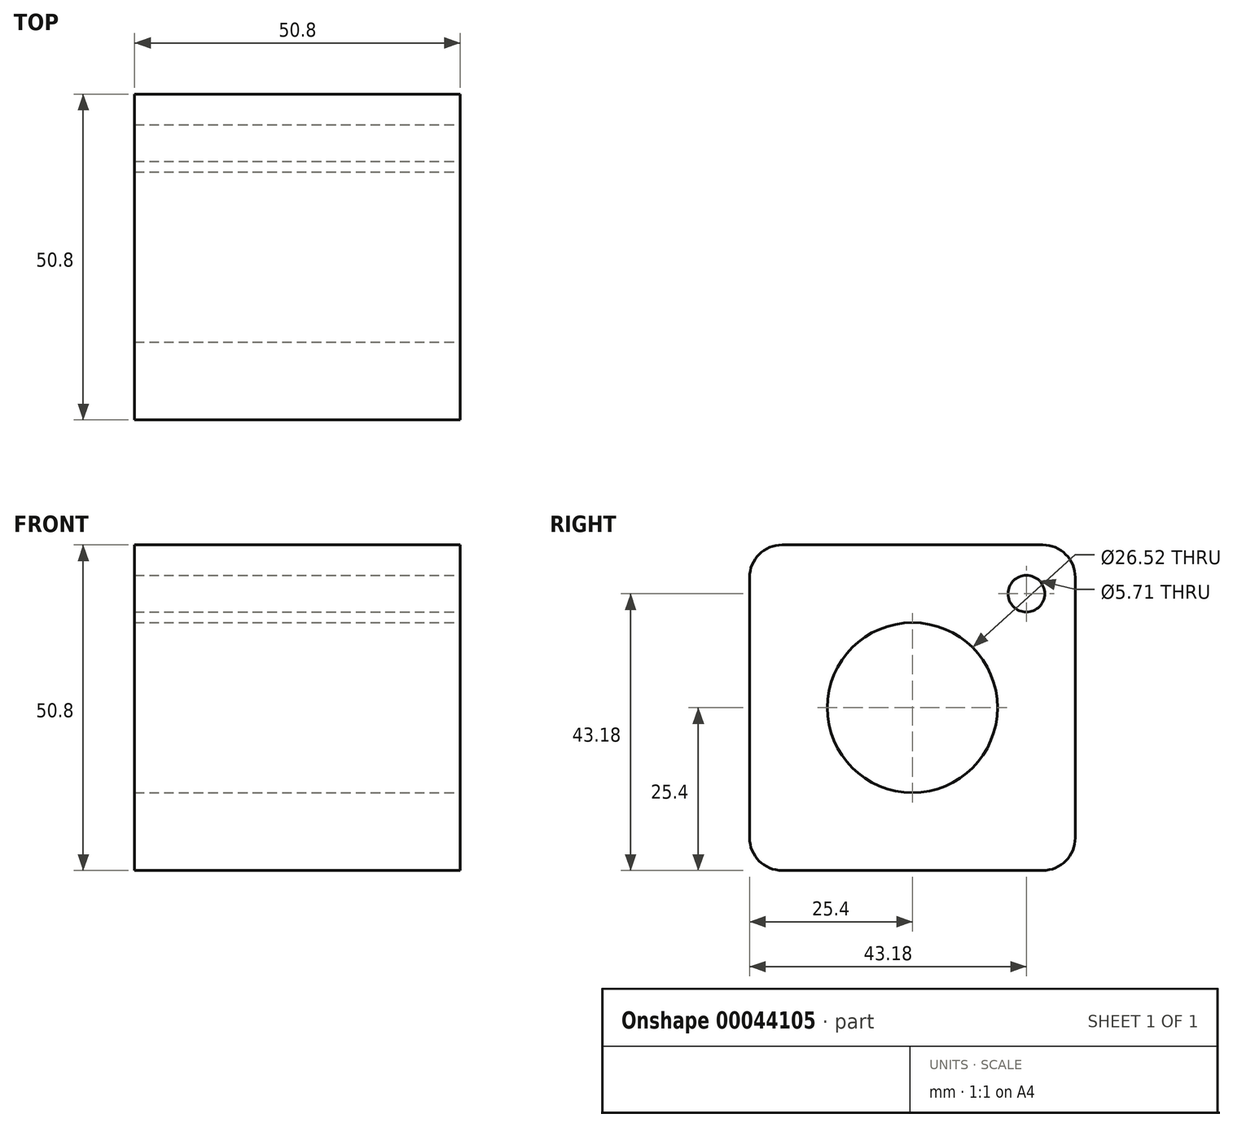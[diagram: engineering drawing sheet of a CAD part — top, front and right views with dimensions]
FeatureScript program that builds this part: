
annotation { "Feature Type Name" : "Feature", "Feature Type Description" : "" }
export const myFeature = defineFeature(function(context is Context, id is Id, definition is map)
    precondition{}
    {
        {
            var Q0;
            Q0=qCreatedBy(makeId("Top.planeOp"),FACE);
            var sketch = newSketch(context, id + "F0", { "sketchPlane" : qUnion([Q0])});
            skLineSegment(sketch, "E0.bottom", {"start": v(0, 0) * mm, "end": v(50.8, 0) * mm});
            skLineSegment(sketch, "E0.top", {"start": v(0, 50.8) * mm, "end": v(50.8, 50.8) * mm});
            skLineSegment(sketch, "E0.left", {"start": v(0, 0) * mm, "end": v(0, 50.8) * mm});
            skLineSegment(sketch, "E0.right", {"start": v(50.8, 0) * mm, "end": v(50.8, 50.8) * mm});
            skSolve(sketch);
        }
        {
            var Q0;
            Q0=makeQuery(id+"F0.imprint","IMPRINT",FACE,{"disambiguationData":[TD([[makeQuery(id+"F0.imprint","IMPRINT",EDGE,{"derivedFrom":sQuery(id+"F0.wireOp",EDGE,"E0.bottom")}),1.0]])]});
            extrude(context, id + "F1", {"entities" : qUnion([Q0]), "depth" : 50.8 * mm});
        }
        {
            var Q0;
            Q0=makeQuery(id+"F1.opExtrude","SWEPT_FACE",FACE,{"disambiguationData":[OSD([sQuery(id+"F0.wireOp",EDGE,"E0.right")])]});
            var sketch = newSketch(context, id + "F2", { "sketchPlane" : qUnion([Q0])});
            skCircle(sketch, "E1", {"center": v(25.4, 25.4) * mm, "radius": 13.26 * mm});
            skPoint(sketch, "E1.centerSnap0", {"position": v(0, 25.4) * mm});
            skSolve(sketch);
        }
        {
            var Q0;
            Q0=makeQuery(id+"F2.imprint","IMPRINT",FACE,{"disambiguationData":[TD([[makeQuery(id+"F2.imprint","IMPRINT",EDGE,{"derivedFrom":sQuery(id+"F2.wireOp",EDGE,"E1")}),1.0]])]});
            extrude(context, id + "F3", {"entities" : qUnion([Q0]), "operationType" : NewBodyOperationType.REMOVE, "endBound" : BoundingType.THROUGH_ALL, "oppositeDirection" : true, "depth" : 25.4 * mm});
        }
        {
            var Q0;
            Q0=makeQuery(id+"F1.opExtrude","CAP_EDGE",EDGE,{"disambiguationData":[OSD([sQuery(id+"F0.wireOp",EDGE,"E0.top")])],"isStart":false});
            var Q1;
            Q1=makeQuery(id+"F1.opExtrude","CAP_EDGE",EDGE,{"disambiguationData":[OSD([sQuery(id+"F0.wireOp",EDGE,"E0.bottom")])],"isStart":false});
            var Q2;
            Q2=makeQuery(id+"F1.opExtrude","CAP_EDGE",EDGE,{"disambiguationData":[OSD([sQuery(id+"F0.wireOp",EDGE,"E0.top")])],"isStart":true});
            var Q3;
            Q3=makeQuery(id+"F1.opExtrude","CAP_EDGE",EDGE,{"disambiguationData":[OSD([sQuery(id+"F0.wireOp",EDGE,"E0.bottom")])],"isStart":true});
            fillet(context, id + "F4", {"entities" : qUnion([Q0, Q1, Q2, Q3]), "radius" : 5.08 * mm, "tangentPropagation" : true, "allowEdgeOverflow" : false});
        }
        {
            var Q0;
            Q0=makeQuery(id+"F1.opExtrude","SWEPT_FACE",FACE,{"disambiguationData":[OSD([sQuery(id+"F0.wireOp",EDGE,"E0.right")])]});
            var sketch = newSketch(context, id + "F5", { "sketchPlane" : qUnion([Q0])});
            skCircle(sketch, "E2", {"center": v(43.18, 43.18) * mm, "radius": 2.86 * mm});
            skSolve(sketch);
        }
        {
            var Q0;
            Q0=makeQuery(id+"F5.imprint","IMPRINT",FACE,{"disambiguationData":[TD([[makeQuery(id+"F5.imprint","IMPRINT",EDGE,{"derivedFrom":sQuery(id+"F5.wireOp",EDGE,"E2")}),1.0]])]});
            extrude(context, id + "F6", {"entities" : qUnion([Q0]), "operationType" : NewBodyOperationType.REMOVE, "endBound" : BoundingType.THROUGH_ALL, "oppositeDirection" : true, "depth" : 25.4 * mm});
        }
    });
